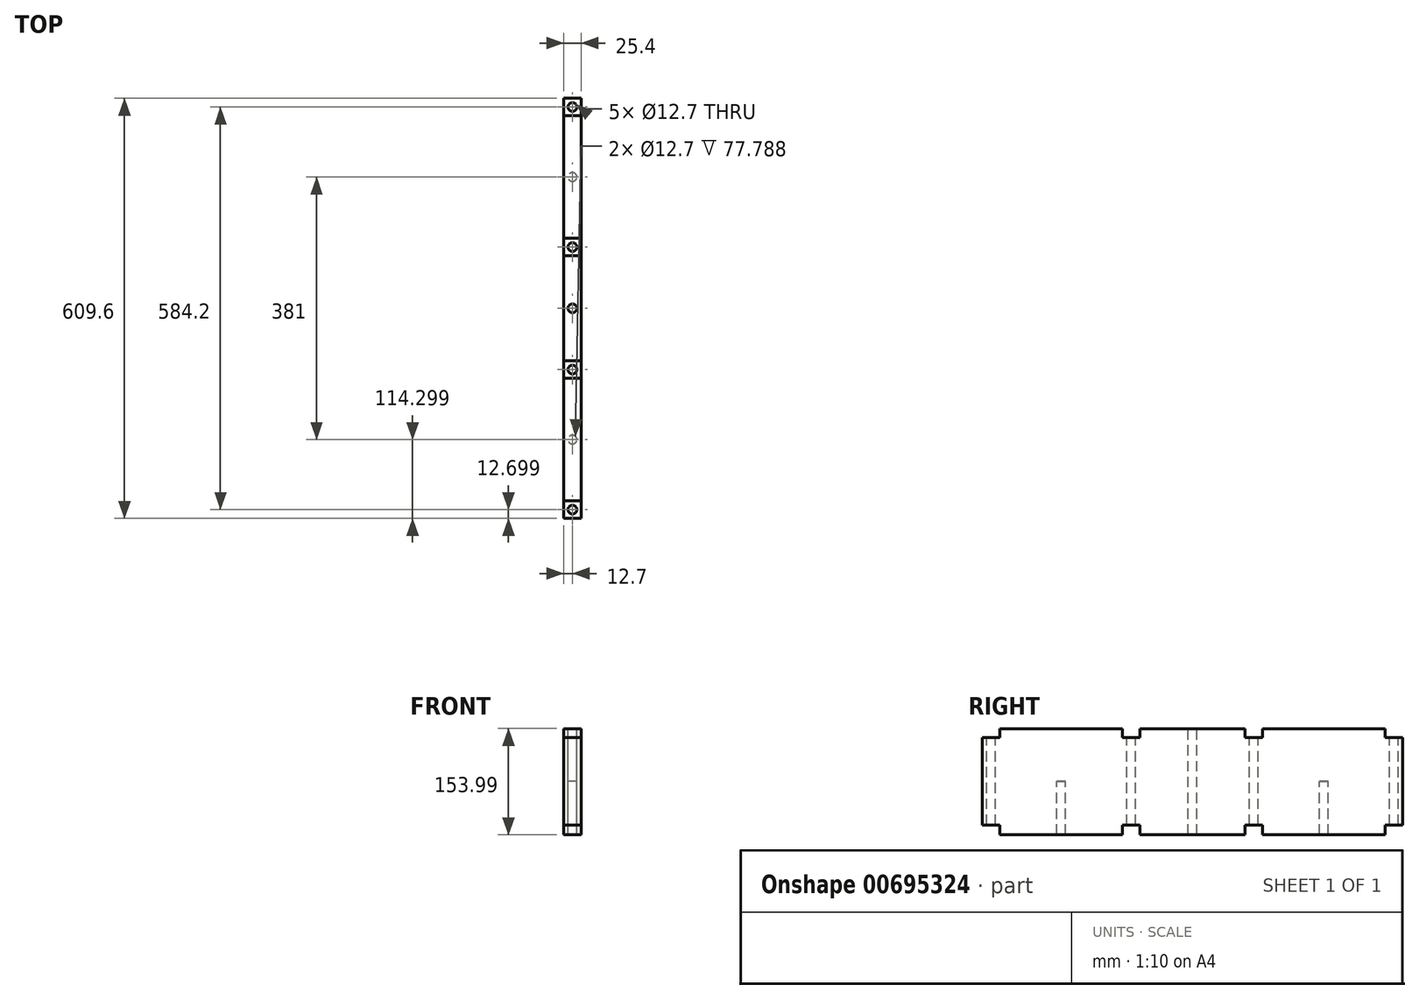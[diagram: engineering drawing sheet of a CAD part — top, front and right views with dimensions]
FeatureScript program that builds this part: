
annotation { "Feature Type Name" : "Feature", "Feature Type Description" : "" }
export const myFeature = defineFeature(function(context is Context, id is Id, definition is map)
    precondition{}
    {
        {
            var Q0;
            Q0=qCreatedBy(makeId("Right.planeOp"),FACE);
            var sketch = newSketch(context, id + "F0", { "sketchPlane" : qUnion([Q0])});
            skLineSegment(sketch, "E0.bottom", {"start": v(-308, -56.05) * mm, "end": v(301.6, -56.05) * mm});
            skLineSegment(sketch, "E0.top", {"start": v(-308, -210.04) * mm, "end": v(301.6, -210.04) * mm});
            skLineSegment(sketch, "E0.left", {"start": v(-308, -56.05) * mm, "end": v(-308, -210.04) * mm});
            skLineSegment(sketch, "E0.right", {"start": v(301.6, -56.05) * mm, "end": v(301.6, -210.04) * mm});
            skSolve(sketch);
        }
        {
            var Q0;
            Q0=makeQuery(id+"F0.imprint","IMPRINT",FACE,{"disambiguationData":[TD([[makeQuery(id+"F0.imprint","IMPRINT",EDGE,{"derivedFrom":sQuery(id+"F0.wireOp",EDGE,"E0.bottom")}),-1.0]])]});
            extrude(context, id + "F1", {"entities" : qUnion([Q0]), "depth" : 25.4 * mm, "offsetDistance" : 25.4 * mm});
        }
        {
            var Q0;
            Q0=makeQuery(id+"F1.opExtrude","CAP_FACE",FACE,{"disambiguationData":[OSD([sQuery(id+"F0.wireOp",EDGE,"E0.bottom"),sQuery(id+"F0.wireOp",EDGE,"E0.top"),sQuery(id+"F0.wireOp",EDGE,"E0.left"),sQuery(id+"F0.wireOp",EDGE,"E0.right")])],"isStart":false});
            var sketch = newSketch(context, id + "F2", { "sketchPlane" : qUnion([Q0])});
            skLineSegment(sketch, "E1.bottom", {"start": v(-308, -210.04) * mm, "end": v(-282.6, -210.04) * mm});
            skLineSegment(sketch, "E1.top", {"start": v(-308, -194.17) * mm, "end": v(-282.6, -194.17) * mm});
            skLineSegment(sketch, "E1.left", {"start": v(-308, -210.04) * mm, "end": v(-308, -194.17) * mm});
            skLineSegment(sketch, "E1.right", {"start": v(-282.6, -210.04) * mm, "end": v(-282.6, -194.17) * mm});
            skLineSegment(sketch, "E2.bottom", {"start": v(-104.8, -210.04) * mm, "end": v(-79.4, -210.04) * mm});
            skLineSegment(sketch, "E2.top", {"start": v(-104.8, -194.17) * mm, "end": v(-79.4, -194.17) * mm});
            skLineSegment(sketch, "E2.left", {"start": v(-104.8, -210.04) * mm, "end": v(-104.8, -194.17) * mm});
            skLineSegment(sketch, "E2.right", {"start": v(-79.4, -210.04) * mm, "end": v(-79.4, -194.17) * mm});
            skLineSegment(sketch, "E3.bottom", {"start": v(73, -210.04) * mm, "end": v(98.4, -210.04) * mm});
            skLineSegment(sketch, "E3.top", {"start": v(73, -194.17) * mm, "end": v(98.4, -194.17) * mm});
            skLineSegment(sketch, "E3.left", {"start": v(73, -210.04) * mm, "end": v(73, -194.17) * mm});
            skLineSegment(sketch, "E3.right", {"start": v(98.4, -210.04) * mm, "end": v(98.4, -194.17) * mm});
            skLineSegment(sketch, "E4.bottom", {"start": v(301.6, -210.04) * mm, "end": v(276.2, -210.04) * mm});
            skLineSegment(sketch, "E4.top", {"start": v(301.6, -194.17) * mm, "end": v(276.2, -194.17) * mm});
            skLineSegment(sketch, "E4.left", {"start": v(301.6, -210.04) * mm, "end": v(301.6, -194.17) * mm});
            skLineSegment(sketch, "E4.right", {"start": v(276.2, -210.04) * mm, "end": v(276.2, -194.17) * mm});
            skLineSegment(sketch, "E5.bottom", {"start": v(-308, -56.05) * mm, "end": v(-282.6, -56.05) * mm});
            skLineSegment(sketch, "E5.top", {"start": v(-308, -68.75) * mm, "end": v(-282.6, -68.75) * mm});
            skLineSegment(sketch, "E5.left", {"start": v(-308, -56.05) * mm, "end": v(-308, -68.75) * mm});
            skLineSegment(sketch, "E5.right", {"start": v(-282.6, -56.05) * mm, "end": v(-282.6, -68.75) * mm});
            skLineSegment(sketch, "E6.bottom", {"start": v(-104.8, -56.05) * mm, "end": v(-79.4, -56.05) * mm});
            skLineSegment(sketch, "E6.top", {"start": v(-104.8, -68.75) * mm, "end": v(-79.4, -68.75) * mm});
            skLineSegment(sketch, "E6.left", {"start": v(-104.8, -56.05) * mm, "end": v(-104.8, -68.75) * mm});
            skLineSegment(sketch, "E6.right", {"start": v(-79.4, -56.05) * mm, "end": v(-79.4, -68.75) * mm});
            skLineSegment(sketch, "E7.bottom", {"start": v(73, -56.05) * mm, "end": v(98.4, -56.05) * mm});
            skLineSegment(sketch, "E7.top", {"start": v(73, -68.75) * mm, "end": v(98.4, -68.75) * mm});
            skLineSegment(sketch, "E7.left", {"start": v(73, -56.05) * mm, "end": v(73, -68.75) * mm});
            skLineSegment(sketch, "E7.right", {"start": v(98.4, -56.05) * mm, "end": v(98.4, -68.75) * mm});
            skLineSegment(sketch, "E8.bottom", {"start": v(301.6, -56.05) * mm, "end": v(276.2, -56.05) * mm});
            skLineSegment(sketch, "E8.top", {"start": v(301.6, -68.75) * mm, "end": v(276.2, -68.75) * mm});
            skLineSegment(sketch, "E8.left", {"start": v(301.6, -56.05) * mm, "end": v(301.6, -68.75) * mm});
            skLineSegment(sketch, "E8.right", {"start": v(276.2, -56.05) * mm, "end": v(276.2, -68.75) * mm});
            skSolve(sketch);
        }
        {
            var Q0;
            Q0=makeQuery(id+"F2.imprint","IMPRINT",FACE,{"disambiguationData":[TD([[makeQuery(id+"F2.imprint","IMPRINT",EDGE,{"derivedFrom":sQuery(id+"F2.wireOp",EDGE,"E5.bottom")}),-1.0]])]});
            var Q1;
            Q1=makeQuery(id+"F2.imprint","IMPRINT",FACE,{"disambiguationData":[TD([[makeQuery(id+"F2.imprint","IMPRINT",EDGE,{"derivedFrom":sQuery(id+"F2.wireOp",EDGE,"E1.bottom")}),1.0]])]});
            var Q2;
            Q2=makeQuery(id+"F2.imprint","IMPRINT",FACE,{"disambiguationData":[TD([[makeQuery(id+"F2.imprint","IMPRINT",EDGE,{"derivedFrom":sQuery(id+"F2.wireOp",EDGE,"E2.bottom")}),1.0]])]});
            var Q3;
            Q3=makeQuery(id+"F2.imprint","IMPRINT",FACE,{"disambiguationData":[TD([[makeQuery(id+"F2.imprint","IMPRINT",EDGE,{"derivedFrom":sQuery(id+"F2.wireOp",EDGE,"E6.bottom")}),-1.0]])]});
            var Q4;
            Q4=makeQuery(id+"F2.imprint","IMPRINT",FACE,{"disambiguationData":[TD([[makeQuery(id+"F2.imprint","IMPRINT",EDGE,{"derivedFrom":sQuery(id+"F2.wireOp",EDGE,"E7.bottom")}),-1.0]])]});
            var Q5;
            Q5=makeQuery(id+"F2.imprint","IMPRINT",FACE,{"disambiguationData":[TD([[makeQuery(id+"F2.imprint","IMPRINT",EDGE,{"derivedFrom":sQuery(id+"F2.wireOp",EDGE,"E3.bottom")}),1.0]])]});
            var Q6;
            Q6=makeQuery(id+"F2.imprint","IMPRINT",FACE,{"disambiguationData":[TD([[makeQuery(id+"F2.imprint","IMPRINT",EDGE,{"derivedFrom":sQuery(id+"F2.wireOp",EDGE,"E8.bottom")}),-1.0]])]});
            var Q7;
            Q7=makeQuery(id+"F2.imprint","IMPRINT",FACE,{"disambiguationData":[TD([[makeQuery(id+"F2.imprint","IMPRINT",EDGE,{"derivedFrom":sQuery(id+"F2.wireOp",EDGE,"E4.bottom")}),1.0]])]});
            extrude(context, id + "F3", {"entities" : qUnion([Q0, Q1, Q2, Q3, Q4, Q5, Q6, Q7]), "operationType" : NewBodyOperationType.REMOVE, "oppositeDirection" : true, "depth" : 25.4 * mm, "offsetDistance" : 25.4 * mm});
        }
        {
            var Q0;
            Q0=makeQuery(id+"F3.boolean.opBoolean","COPY",FACE,{"derivedFrom":makeQuery(id+"F3.opExtrude","SWEPT_FACE",FACE,{"disambiguationData":[OSD([sQuery(id+"F2.wireOp",EDGE,"E5.top")])]})});
            var sketch = newSketch(context, id + "F4", { "sketchPlane" : qUnion([Q0])});
            skCircle(sketch, "E9", {"center": v(12.7, -295.3) * mm, "radius": 6.35 * mm});
            skPoint(sketch, "E9.centerSnap0", {"position": v(25.4, -295.3) * mm});
            skPoint(sketch, "E9.centerSnap1", {"position": v(12.7, -308) * mm});
            skSolve(sketch);
        }
        {
            var Q0;
            Q0=makeQuery(id+"F3.boolean.opBoolean","COPY",FACE,{"derivedFrom":makeQuery(id+"F3.opExtrude","SWEPT_FACE",FACE,{"disambiguationData":[OSD([sQuery(id+"F2.wireOp",EDGE,"E6.top")])]})});
            var sketch = newSketch(context, id + "F5", { "sketchPlane" : qUnion([Q0])});
            skCircle(sketch, "E10", {"center": v(12.7, -92.1) * mm, "radius": 6.35 * mm});
            skPoint(sketch, "E10.centerSnap0", {"position": v(25.4, -92.1) * mm});
            skPoint(sketch, "E10.centerSnap1", {"position": v(12.7, -79.4) * mm});
            skSolve(sketch);
        }
        {
            var Q0;
            Q0=makeQuery(id+"F3.boolean.opBoolean","COPY",FACE,{"derivedFrom":makeQuery(id+"F3.opExtrude","SWEPT_FACE",FACE,{"disambiguationData":[OSD([sQuery(id+"F2.wireOp",EDGE,"E7.top")])]})});
            var sketch = newSketch(context, id + "F6", { "sketchPlane" : qUnion([Q0])});
            skCircle(sketch, "E11", {"center": v(12.7, 85.7) * mm, "radius": 6.35 * mm});
            skPoint(sketch, "E11.centerSnap0", {"position": v(25.4, 85.7) * mm});
            skPoint(sketch, "E11.centerSnap1", {"position": v(12.7, 98.4) * mm});
            skSolve(sketch);
        }
        {
            var Q0;
            Q0=makeQuery(id+"F3.boolean.opBoolean","COPY",FACE,{"derivedFrom":makeQuery(id+"F3.opExtrude","SWEPT_FACE",FACE,{"disambiguationData":[OSD([sQuery(id+"F2.wireOp",EDGE,"E8.top")])]})});
            var sketch = newSketch(context, id + "F7", { "sketchPlane" : qUnion([Q0])});
            skCircle(sketch, "E12", {"center": v(12.7, 288.9) * mm, "radius": 6.35 * mm});
            skPoint(sketch, "E12.centerSnap0", {"position": v(25.4, 288.9) * mm});
            skPoint(sketch, "E12.centerSnap1", {"position": v(12.7, 301.6) * mm});
            skSolve(sketch);
        }
        {
            var Q0;
            Q0=makeQuery(id+"F7.imprint","IMPRINT",FACE,{"disambiguationData":[TD([[makeQuery(id+"F7.imprint","IMPRINT",EDGE,{"derivedFrom":sQuery(id+"F7.wireOp",EDGE,"E12")}),1.0]])]});
            var Q1;
            Q1=makeQuery(id+"F6.imprint","IMPRINT",FACE,{"disambiguationData":[TD([[makeQuery(id+"F6.imprint","IMPRINT",EDGE,{"derivedFrom":sQuery(id+"F6.wireOp",EDGE,"E11")}),1.0]])]});
            var Q2;
            Q2=makeQuery(id+"F5.imprint","IMPRINT",FACE,{"disambiguationData":[TD([[makeQuery(id+"F5.imprint","IMPRINT",EDGE,{"derivedFrom":sQuery(id+"F5.wireOp",EDGE,"E10")}),1.0]])]});
            var Q3;
            Q3=makeQuery(id+"F4.imprint","IMPRINT",FACE,{"disambiguationData":[TD([[makeQuery(id+"F4.imprint","IMPRINT",EDGE,{"derivedFrom":sQuery(id+"F4.wireOp",EDGE,"E9")}),1.0]])]});
            extrude(context, id + "F8", {"entities" : qUnion([Q0, Q1, Q2, Q3]), "operationType" : NewBodyOperationType.REMOVE, "oppositeDirection" : true, "depth" : 177.8 * mm, "offsetDistance" : 25.4 * mm});
        }
        {
            var Q0;
            Q0=makeQuery(id+"F3.boolean.opBoolean","COPY",FACE,{"derivedFrom":makeQuery(id+"F3.opExtrude","SWEPT_FACE",FACE,{"disambiguationData":[OSD([sQuery(id+"F2.wireOp",EDGE,"E1.top")])]})});
            var Q1;
            Q1=makeQuery(id+"F3.boolean.opBoolean","COPY",FACE,{"derivedFrom":makeQuery(id+"F3.opExtrude","SWEPT_FACE",FACE,{"disambiguationData":[OSD([sQuery(id+"F2.wireOp",EDGE,"E2.top")])]})});
            var Q2;
            Q2=makeQuery(id+"F3.boolean.opBoolean","COPY",FACE,{"derivedFrom":makeQuery(id+"F3.opExtrude","SWEPT_FACE",FACE,{"disambiguationData":[OSD([sQuery(id+"F2.wireOp",EDGE,"E3.top")])]})});
            var Q3;
            Q3=makeQuery(id+"F3.boolean.opBoolean","COPY",FACE,{"derivedFrom":makeQuery(id+"F3.opExtrude","SWEPT_FACE",FACE,{"disambiguationData":[OSD([sQuery(id+"F2.wireOp",EDGE,"E4.top")])]})});
            extrude(context, id + "F9", {"entities" : qUnion([Q0, Q1, Q2, Q3]), "operationType" : NewBodyOperationType.ADD, "depth" : 1.59 * mm, "offsetDistance" : 25.4 * mm});
        }
        {
            var Q0;
            {var subQ3=sQuery(id+"F0.wireOp",EDGE,"E0.bottom");Q0=makeQuery(id+"F3.boolean.opBoolean","SPLIT",FACE,{"disambiguationData":[TD([makeQuery(id+"F3.opExtrude","SWEPT_FACE",FACE,{"disambiguationData":[OSD([sQuery(id+"F2.wireOp",EDGE,"E7.right")])]})])],"derivedFrom":makeQuery(id+"F1.opExtrude","SWEPT_FACE",FACE,{"disambiguationData":[OSD([subQ3])]})});}
            var sketch = newSketch(context, id + "F10", { "sketchPlane" : qUnion([Q0])});
            skCircle(sketch, "E13", {"center": v(12.7, 187.3) * mm, "radius": 6.35 * mm});
            skPoint(sketch, "E13.centerSnap0", {"position": v(0, 187.3) * mm});
            skPoint(sketch, "E13.centerSnap1", {"position": v(12.7, 276.2) * mm});
            skSolve(sketch);
        }
        {
            var Q0;
            {var subQ3=sQuery(id+"F0.wireOp",EDGE,"E0.bottom");Q0=makeQuery(id+"F3.boolean.opBoolean","SPLIT",FACE,{"disambiguationData":[TD([makeQuery(id+"F3.opExtrude","SWEPT_FACE",FACE,{"disambiguationData":[OSD([sQuery(id+"F2.wireOp",EDGE,"E6.right")])]})])],"derivedFrom":makeQuery(id+"F1.opExtrude","SWEPT_FACE",FACE,{"disambiguationData":[OSD([subQ3])]})});}
            var sketch = newSketch(context, id + "F11", { "sketchPlane" : qUnion([Q0])});
            skCircle(sketch, "E14", {"center": v(12.7, -3.2) * mm, "radius": 6.35 * mm});
            skPoint(sketch, "E14.centerSnap0", {"position": v(12.7, 73) * mm});
            skPoint(sketch, "E14.centerSnap1", {"position": v(0, -3.2) * mm});
            skSolve(sketch);
        }
        {
            var Q0;
            {var subQ3=sQuery(id+"F0.wireOp",EDGE,"E0.bottom");Q0=makeQuery(id+"F3.boolean.opBoolean","SPLIT",FACE,{"disambiguationData":[TD([makeQuery(id+"F3.opExtrude","SWEPT_FACE",FACE,{"disambiguationData":[OSD([sQuery(id+"F2.wireOp",EDGE,"E5.right")])]})])],"derivedFrom":makeQuery(id+"F1.opExtrude","SWEPT_FACE",FACE,{"disambiguationData":[OSD([subQ3])]})});}
            var sketch = newSketch(context, id + "F12", { "sketchPlane" : qUnion([Q0])});
            skCircle(sketch, "E15", {"center": v(12.7, -193.7) * mm, "radius": 6.35 * mm});
            skPoint(sketch, "E15.centerSnap0", {"position": v(0, -193.7) * mm});
            skPoint(sketch, "E15.centerSnap1", {"position": v(12.7, -104.8) * mm});
            skSolve(sketch);
        }
        {
            var Q0;
            Q0=makeQuery(id+"F12.imprint","IMPRINT",FACE,{"disambiguationData":[TD([[makeQuery(id+"F12.imprint","IMPRINT",EDGE,{"derivedFrom":sQuery(id+"F12.wireOp",EDGE,"E15")}),1.0]])]});
            var Q1;
            Q1=makeQuery(id+"F11.imprint","IMPRINT",FACE,{"disambiguationData":[TD([[makeQuery(id+"F11.imprint","IMPRINT",EDGE,{"derivedFrom":sQuery(id+"F11.wireOp",EDGE,"E14")}),1.0]])]});
            var Q2;
            Q2=makeQuery(id+"F10.imprint","IMPRINT",FACE,{"disambiguationData":[TD([[makeQuery(id+"F10.imprint","IMPRINT",EDGE,{"derivedFrom":sQuery(id+"F10.wireOp",EDGE,"E13")}),1.0]])]});
            extrude(context, id + "F13", {"entities" : qUnion([Q0, Q1, Q2]), "operationType" : NewBodyOperationType.REMOVE, "oppositeDirection" : true, "depth" : 177.8 * mm, "offsetDistance" : 25.4 * mm});
        }
        {
            var Q0;
            {var subQ0=sQuery(id+"F2.wireOp",EDGE,"E4.top");var subQ1=sQuery(id+"F2.wireOp",EDGE,"E3.top");var subQ2=sQuery(id+"F2.wireOp",EDGE,"E2.top");var subQ3=sQuery(id+"F2.wireOp",EDGE,"E1.top");Q0=makeQuery(id+"F9.boolean.opBoolean","MERGE",FACE,{"derivedFrom":[makeQuery(id+"F1.opExtrude","CAP_FACE",FACE,{"disambiguationData":[OSD([sQuery(id+"F0.wireOp",EDGE,"E0.bottom"),sQuery(id+"F0.wireOp",EDGE,"E0.top"),sQuery(id+"F0.wireOp",EDGE,"E0.left"),sQuery(id+"F0.wireOp",EDGE,"E0.right")])],"isStart":false}),makeQuery(id+"F9.opExtrude","SWEPT_FACE",FACE,{"disambiguationData":[OSD([subQ3]),TDD([makeQuery(id+"F3.boolean.opBoolean","COPY",EDGE,{"derivedFrom":makeQuery(id+"F3.opExtrude","CAP_EDGE",EDGE,{"disambiguationData":[OSD([subQ3])],"isStart":true})})])]}),makeQuery(id+"F9.opExtrude","SWEPT_FACE",FACE,{"disambiguationData":[OSD([subQ2]),TDD([makeQuery(id+"F3.boolean.opBoolean","COPY",EDGE,{"derivedFrom":makeQuery(id+"F3.opExtrude","CAP_EDGE",EDGE,{"disambiguationData":[OSD([subQ2])],"isStart":true})})])]}),makeQuery(id+"F9.opExtrude","SWEPT_FACE",FACE,{"disambiguationData":[OSD([subQ1]),TDD([makeQuery(id+"F3.boolean.opBoolean","COPY",EDGE,{"derivedFrom":makeQuery(id+"F3.opExtrude","CAP_EDGE",EDGE,{"disambiguationData":[OSD([subQ1])],"isStart":true})})])]}),makeQuery(id+"F9.opExtrude","SWEPT_FACE",FACE,{"disambiguationData":[OSD([subQ0]),TDD([makeQuery(id+"F3.boolean.opBoolean","COPY",EDGE,{"derivedFrom":makeQuery(id+"F3.opExtrude","CAP_EDGE",EDGE,{"disambiguationData":[OSD([subQ0])],"isStart":true})})])]})]});}
            var sketch = newSketch(context, id + "F14", { "sketchPlane" : qUnion([Q0])});
            skCircle(sketch, "E16", {"center": v(-193.7, -132.25) * mm, "radius": 25.4 * mm});
            skPoint(sketch, "E16.centerSnap0", {"position": v(-308, -132.25) * mm});
            skPoint(sketch, "E16.centerSnap1", {"position": v(-193.7, -56.05) * mm});
            skCircle(sketch, "E17", {"center": v(187.3, -132.25) * mm, "radius": 25.4 * mm});
            skPoint(sketch, "E17.centerSnap0", {"position": v(187.3, -56.05) * mm});
            skPoint(sketch, "E17.centerSnap1", {"position": v(301.6, -132.25) * mm});
            skSolve(sketch);
        }
        {
            var Q0;
            Q0=makeQuery(id+"F14.imprint","IMPRINT",FACE,{"disambiguationData":[TD([[makeQuery(id+"F14.imprint","IMPRINT",EDGE,{"derivedFrom":sQuery(id+"F14.wireOp",EDGE,"E16")}),1.0]])]});
            var Q1;
            Q1=makeQuery(id+"F14.imprint","IMPRINT",FACE,{"disambiguationData":[TD([[makeQuery(id+"F14.imprint","IMPRINT",EDGE,{"derivedFrom":sQuery(id+"F14.wireOp",EDGE,"E17")}),1.0]])]});
            extrude(context, id + "F15", {"entities" : qUnion([Q0, Q1]), "operationType" : NewBodyOperationType.REMOVE, "oppositeDirection" : true, "depth" : 25.4 * mm, "offsetDistance" : 25.4 * mm});
        }
        {
            var Q0;
            Q0=makeQuery(id+"F12.imprint","IMPRINT",FACE,{"disambiguationData":[TD([[makeQuery(id+"F12.imprint","IMPRINT",EDGE,{"derivedFrom":sQuery(id+"F12.wireOp",EDGE,"E15")}),1.0]])]});
            extrude(context, id + "F16", {"entities" : qUnion([Q0]), "operationType" : NewBodyOperationType.ADD, "oppositeDirection" : true, "depth" : 76.2 * mm, "offsetDistance" : 25.4 * mm});
        }
        {
            var Q0;
            Q0=makeQuery(id+"F10.imprint","IMPRINT",FACE,{"disambiguationData":[TD([[makeQuery(id+"F10.imprint","IMPRINT",EDGE,{"derivedFrom":sQuery(id+"F10.wireOp",EDGE,"E13")}),1.0]])]});
            extrude(context, id + "F17", {"entities" : qUnion([Q0]), "operationType" : NewBodyOperationType.ADD, "oppositeDirection" : true, "depth" : 76.2 * mm, "offsetDistance" : 25.4 * mm});
        }
        {
            var Q0;
            Q0=makeQuery(id+"F14.imprint","IMPRINT",FACE,{"disambiguationData":[TD([[makeQuery(id+"F14.imprint","IMPRINT",EDGE,{"derivedFrom":sQuery(id+"F14.wireOp",EDGE,"E17")}),1.0]])]});
            extrude(context, id + "F18", {"entities" : qUnion([Q0]), "operationType" : NewBodyOperationType.REMOVE, "oppositeDirection" : true, "depth" : 25.4 * mm, "offsetDistance" : 25.4 * mm});
        }
        {
            var Q0;
            Q0=makeQuery(id+"F14.imprint","IMPRINT",FACE,{"disambiguationData":[TD([[makeQuery(id+"F14.imprint","IMPRINT",EDGE,{"derivedFrom":sQuery(id+"F14.wireOp",EDGE,"E16")}),1.0]])]});
            extrude(context, id + "F19", {"entities" : qUnion([Q0]), "operationType" : NewBodyOperationType.REMOVE, "oppositeDirection" : true, "depth" : 25.4 * mm, "offsetDistance" : 25.4 * mm});
        }
    });
